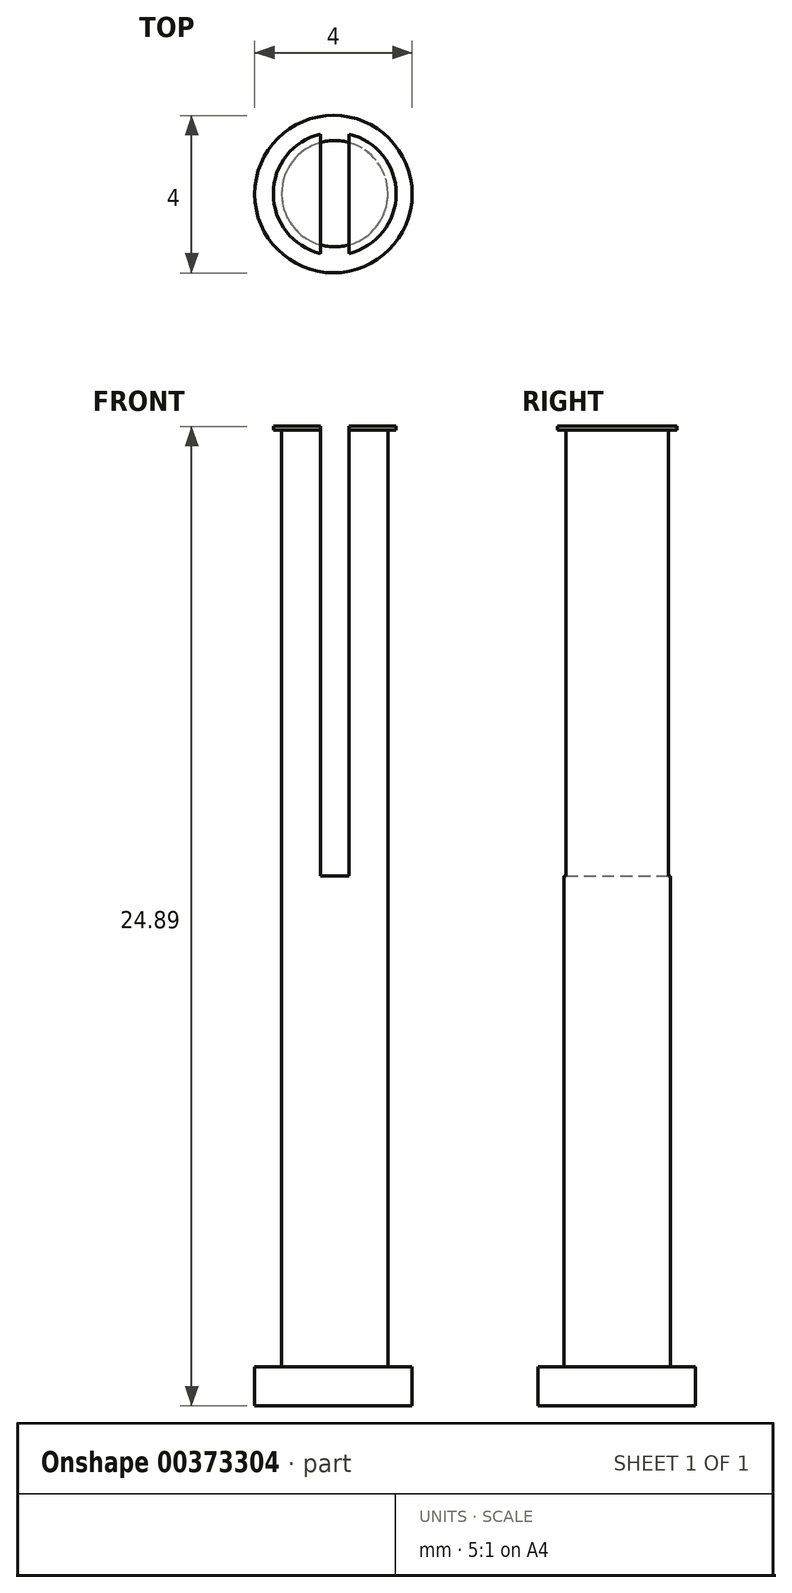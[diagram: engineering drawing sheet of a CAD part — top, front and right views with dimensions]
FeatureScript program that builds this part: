
annotation { "Feature Type Name" : "Feature", "Feature Type Description" : "" }
export const myFeature = defineFeature(function(context is Context, id is Id, definition is map)
    precondition{}
    {
        {
            var Q0;
            Q0=qCreatedBy(makeId("Top.planeOp"),FACE);
            var sketch = newSketch(context, id + "F0", { "sketchPlane" : qUnion([Q0])});
            skCircle(sketch, "E0", {"center": v(-9.96, 16) * mm, "radius": 2 * mm});
            skSolve(sketch);
        }
        {
            var Q0;
            Q0=makeQuery(id+"F0.imprint","IMPRINT",FACE,{"disambiguationData":[TD([[makeQuery(id+"F0.imprint","IMPRINT",EDGE,{"derivedFrom":sQuery(id+"F0.wireOp",EDGE,"E0")}),1.0]])]});
            extrude(context, id + "F1", {"entities" : qUnion([Q0]), "depth" : 1 * mm});
        }
        {
            var Q0;
            Q0=makeQuery(id+"F0.imprint","IMPRINT",FACE,{"disambiguationData":[TD([[makeQuery(id+"F0.imprint","IMPRINT",EDGE,{"derivedFrom":sQuery(id+"F0.wireOp",EDGE,"E0")}),1.0]])]});
            var sketch = newSketch(context, id + "F2", { "sketchPlane" : qUnion([Q0])});
            skCircle(sketch, "E1", {"center": v(-9.93, 16) * mm, "radius": 1.35 * mm});
            skSolve(sketch);
        }
        {
            var Q0;
            Q0 = qSketchRegion(id + "F2", true);
            extrude(context, id + "F3", {"entities" : qUnion([Q0]), "operationType" : NewBodyOperationType.ADD, "depth" : 24.9 * mm});
        }
        {
            var Q0;
            {var subQ0=sQuery(id+"F2.wireOp",EDGE,"E1");Q0=makeQuery(id+"Fctqj8N5RYF67pz_1.boolean.opBoolean","SPLIT",FACE,{"disambiguationData":[TD([makeQuery(id+"Fctqj8N5RYF67pz_1.opExtrude","SWEPT_FACE",FACE,{"disambiguationData":[OSD([sQuery(id+"Fkm6xzE5y74ZPrF_1.wireOp",EDGE,"qD4ypYh9-JU0T-cYaQ-3JcL-f8i0TwQcLX6L.left")])]})])],"derivedFrom":makeQuery(id+"F3.opExtrude","CAP_FACE",FACE,{"disambiguationData":[OSD([subQ0])],"isStart":false})});}
            var sketch = newSketch(context, id + "F4", { "sketchPlane" : qUnion([Q0])});
            skCircle(sketch, "E2", {"center": v(-9.93, 16) * mm, "radius": 1.56 * mm});
            skSolve(sketch);
        }
        {
            var Q0;
            Q0=makeQuery(id+"F4.imprint","IMPRINT",FACE,{"disambiguationData":[TD([[makeQuery(id+"F4.imprint","IMPRINT",EDGE,{"derivedFrom":sQuery(id+"F4.wireOp",EDGE,"E2")}),1.0]])]});
            extrude(context, id + "F5", {"entities" : qUnion([Q0]), "operationType" : NewBodyOperationType.ADD, "oppositeDirection" : true, "depth" : 0.1 * mm});
        }
        {
            var Q0;
            {var subQ0=sQuery(id+"F2.wireOp",EDGE,"E1");Q0=makeQuery(id+"F5.boolean.opBoolean","MERGE",FACE,{"derivedFrom":[makeQuery(id+"F3.opExtrude","CAP_FACE",FACE,{"disambiguationData":[OSD([subQ0])],"isStart":false}),makeQuery(id+"F5.opExtrude","CAP_FACE",FACE,{"disambiguationData":[OSD([subQ0,sQuery(id+"F4.wireOp",EDGE,"E2")])],"isStart":true})]});}
            var sketch = newSketch(context, id + "F6", { "sketchPlane" : qUnion([Q0])});
            skLineSegment(sketch, "E3.bottom", {"start": v(-9.56, 14.13) * mm, "end": v(-10.3, 14.13) * mm});
            skLineSegment(sketch, "E3.top", {"start": v(-9.56, 17.87) * mm, "end": v(-10.3, 17.87) * mm});
            skLineSegment(sketch, "E3.left", {"start": v(-9.56, 14.13) * mm, "end": v(-9.56, 17.87) * mm});
            skLineSegment(sketch, "E3.right", {"start": v(-10.3, 14.13) * mm, "end": v(-10.3, 17.87) * mm});
            skPoint(sketch, "E3.middle", {"position": v(-9.93, 16) * mm});
            skSolve(sketch);
        }
        {
            var Q0;
            {var subQ0=sQuery(id+"F6.wireOp",EDGE,"E3.left");var subQ1=makeQuery(id+"F5.opExtrude","CAP_EDGE",EDGE,{"disambiguationData":[OSD([sQuery(id+"F4.wireOp",EDGE,"E2")])],"isStart":true});var subQ2=makeQuery(id+"F6.imprint","INTERSECT",VERTEX,{"disambiguationData":[OD(0.0)],"derivedFrom":[subQ1,subQ0]});Q0=makeQuery(id+"F6.imprint","IMPRINT",FACE,{"disambiguationData":[TD([[makeQuery(id+"F6.imprint","IMPRINT",EDGE,{"disambiguationData":[TD([[subQ2,-1.0]])],"derivedFrom":subQ0}),1.0]])]});}
            extrude(context, id + "F7", {"entities" : qUnion([Q0]), "operationType" : NewBodyOperationType.REMOVE, "oppositeDirection" : true, "depth" : 11.43 * mm});
        }
    });
